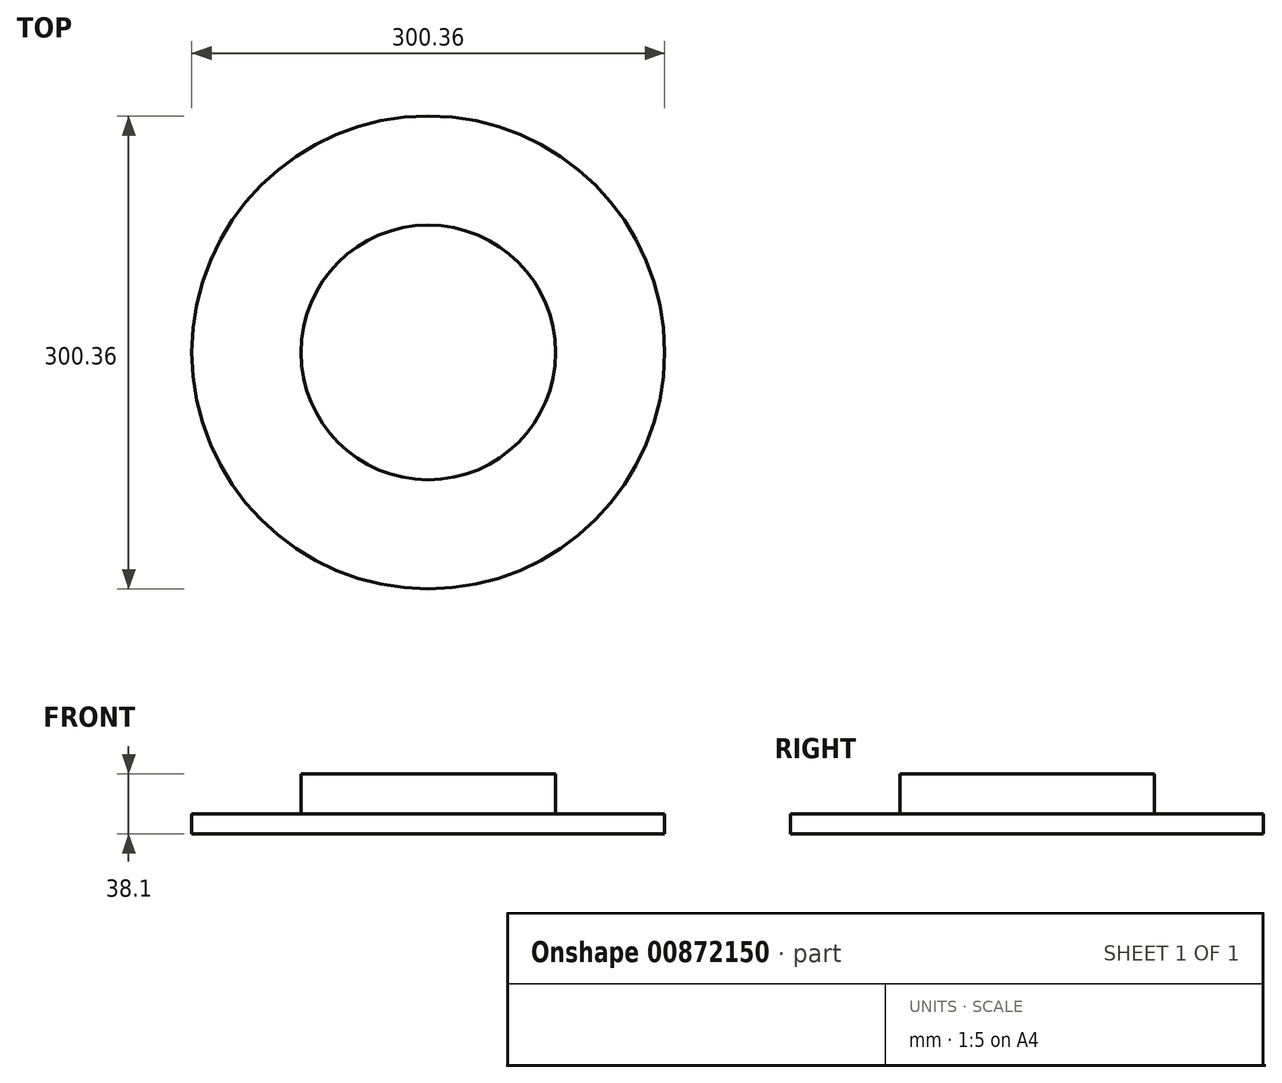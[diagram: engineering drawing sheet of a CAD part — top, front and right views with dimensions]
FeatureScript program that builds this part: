
annotation { "Feature Type Name" : "Feature", "Feature Type Description" : "" }
export const myFeature = defineFeature(function(context is Context, id is Id, definition is map)
    precondition{}
    {
        {
            var Q0;
            Q0=qCreatedBy(makeId("Top.planeOp"),FACE);
            var sketch = newSketch(context, id + "F0", { "sketchPlane" : qUnion([Q0])});
            skCircle(sketch, "E0", {"center": v(0, 0) * mm, "radius": 150.18 * mm});
            skSolve(sketch);
        }
        {
            var Q0;
            Q0=qCreatedBy(makeId("Top.planeOp"),FACE);
            var sketch = newSketch(context, id + "F1", { "sketchPlane" : qUnion([Q0])});
            skCircle(sketch, "E1", {"center": v(0, 0) * mm, "radius": 80.86 * mm});
            skSolve(sketch);
        }
        {
            var Q0;
            Q0 = qSketchRegion(id + "F1", true);
            var Q1;
            Q1=sQuery(id+"F1.wireOp",EDGE,"E1");
            extrude(context, id + "F2", {"entities" : qUnion([Q0]), "surfaceEntities" : qUnion([Q1]), "depth" : 25.4 * mm, "offsetDistance" : 25.4 * mm});
        }
        {
            var Q0;
            Q0=makeQuery(id+"F0.imprint","IMPRINT",FACE,{"disambiguationData":[TD([[makeQuery(id+"F0.imprint","IMPRINT",EDGE,{"derivedFrom":sQuery(id+"F0.wireOp",EDGE,"E0")}),1.0]])]});
            var Q1;
            Q1=sQuery(id+"F0.wireOp",EDGE,"E0");
            extrude(context, id + "F3", {"entities" : qUnion([Q0]), "operationType" : NewBodyOperationType.ADD, "surfaceEntities" : qUnion([Q1]), "depth" : -12.7 * mm, "offsetDistance" : 25.4 * mm});
        }
    });
